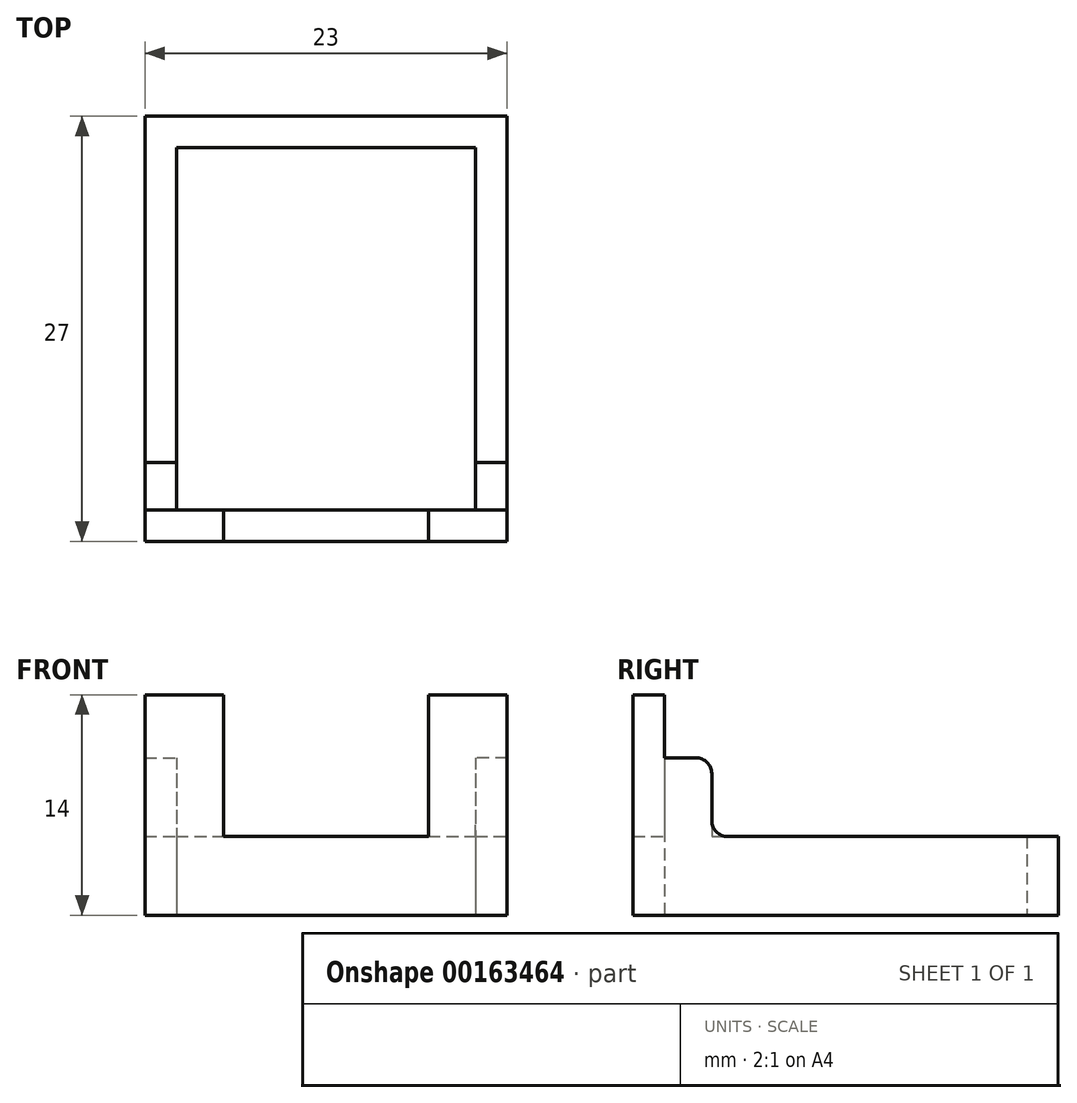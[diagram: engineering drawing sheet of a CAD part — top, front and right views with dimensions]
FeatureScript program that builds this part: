
annotation { "Feature Type Name" : "Feature", "Feature Type Description" : "" }
export const myFeature = defineFeature(function(context is Context, id is Id, definition is map)
    precondition{}
    {
        {
            var Q0;
            Q0=qCreatedBy(makeId("Top.planeOp"),FACE);
            var sketch = newSketch(context, id + "F0", { "sketchPlane" : qUnion([Q0])});
            skLineSegment(sketch, "E0", {"start": v(0, 0) * mm, "end": v(0, 23) * mm});
            skLineSegment(sketch, "E1", {"start": v(0, 0) * mm, "end": v(19, 0) * mm});
            skLineSegment(sketch, "E2", {"start": v(21, -2) * mm, "end": v(-2, -2) * mm});
            skLineSegment(sketch, "E3", {"start": v(19, 0) * mm, "end": v(19, 23) * mm});
            skLineSegment(sketch, "E4", {"start": v(0, 23) * mm, "end": v(19, 23) * mm});
            skLineSegment(sketch, "E5", {"start": v(-2, 25) * mm, "end": v(21, 25) * mm});
            skLineSegment(sketch, "E6", {"start": v(-2, -2) * mm, "end": v(-2, 25) * mm});
            skLineSegment(sketch, "E7", {"start": v(21, -2) * mm, "end": v(21, 25) * mm});
            skSolve(sketch);
        }
        {
            var Q0;
            Q0=qSketchRegion(id+"F0",true);
            extrude(context, id + "F1", {"entities" : qUnion([Q0]), "depth" : 5 * mm});
        }
        {
            var Q0;
            Q0=makeQuery(id+"F1.opExtrude","CAP_FACE",FACE,{"disambiguationData":[OSD([sQuery(id+"F0.wireOp",EDGE,"E0"),sQuery(id+"F0.wireOp",EDGE,"fMDAZUCE-WxNw-tCVg-Pr7f-gKTRDs7ux1xq"),sQuery(id+"F0.wireOp",EDGE,"E1"),sQuery(id+"F0.wireOp",EDGE,"E2"),sQuery(id+"F0.wireOp",EDGE,"em9QBzyh-X0cC-lrsQ-LOUW-UWbV2uQWN0fi"),sQuery(id+"F0.wireOp",EDGE,"E3"),sQuery(id+"F0.wireOp",EDGE,"HnKAWu8F-w6AE-VERm-Axyq-VS4Tu44atyqC"),sQuery(id+"F0.wireOp",EDGE,"QTcbnend-T0hK-HJJc-kWl9-1F0Q0khNvwRf")])],"isStart":false});
            var sketch = newSketch(context, id + "F2", { "sketchPlane" : qUnion([Q0])});
            skLineSegment(sketch, "E8", {"start": v(0, 0) * mm, "end": v(3, 0) * mm});
            skLineSegment(sketch, "E9", {"start": v(3, 0) * mm, "end": v(3, -2) * mm});
            skLineSegment(sketch, "E10", {"start": v(3, -2) * mm, "end": v(-2, -2) * mm});
            skLineSegment(sketch, "E11", {"start": v(-2, -2) * mm, "end": v(-2, 3) * mm});
            skLineSegment(sketch, "E12", {"start": v(-2, 3) * mm, "end": v(0, 3) * mm});
            skLineSegment(sketch, "E13", {"start": v(0, 3) * mm, "end": v(0, 0) * mm});
            skSolve(sketch);
        }
        {
            var Q0;
            Q0=makeQuery(id+"F2.imprint","IMPRINT",FACE,{"disambiguationData":[TD([[makeQuery(id+"F2.imprint","IMPRINT",EDGE,{"derivedFrom":sQuery(id+"F2.wireOp",EDGE,"E8")}),-1.0]])]});
            extrude(context, id + "F3", {"entities" : qUnion([Q0]), "operationType" : NewBodyOperationType.ADD, "depth" : 5 * mm});
        }
        {
            var Q0;
            {var subQ0=sQuery(id+"F0.wireOp",EDGE,"HnKAWu8F-w6AE-VERm-Axyq-VS4Tu44atyqC");var subQ1=sQuery(id+"F0.wireOp",EDGE,"E3");var subQ2=sQuery(id+"F0.wireOp",EDGE,"E2");var subQ3=sQuery(id+"F0.wireOp",EDGE,"E1");var subQ4=sQuery(id+"F0.wireOp",EDGE,"QTcbnend-T0hK-HJJc-kWl9-1F0Q0khNvwRf");Q0=makeQuery(id+"F3.boolean.opBoolean","SPLIT",FACE,{"disambiguationData":[TD([makeQuery(id+"F1.opExtrude","SWEPT_FACE",FACE,{"disambiguationData":[OSD([subQ3])]})])],"derivedFrom":makeQuery(id+"F1.opExtrude","CAP_FACE",FACE,{"disambiguationData":[OSD([sQuery(id+"F0.wireOp",EDGE,"E0"),sQuery(id+"F0.wireOp",EDGE,"fMDAZUCE-WxNw-tCVg-Pr7f-gKTRDs7ux1xq"),subQ3,subQ2,sQuery(id+"F0.wireOp",EDGE,"em9QBzyh-X0cC-lrsQ-LOUW-UWbV2uQWN0fi"),subQ1,subQ0,subQ4])],"isStart":false})});}
            var sketch = newSketch(context, id + "F4", { "sketchPlane" : qUnion([Q0])});
            skLineSegment(sketch, "E14", {"start": v(19, 0) * mm, "end": v(19, 3) * mm});
            skLineSegment(sketch, "E15", {"start": v(19, 3) * mm, "end": v(21, 3) * mm});
            skLineSegment(sketch, "E16", {"start": v(21, 3) * mm, "end": v(21, -2) * mm});
            skLineSegment(sketch, "E17", {"start": v(21, -2) * mm, "end": v(16, -2) * mm});
            skLineSegment(sketch, "E18", {"start": v(16, -2) * mm, "end": v(16, 0) * mm});
            skLineSegment(sketch, "E19", {"start": v(16, 0) * mm, "end": v(19, 0) * mm});
            skSolve(sketch);
        }
        {
            var Q0;
            Q0=makeQuery(id+"F4.imprint","IMPRINT",FACE,{"disambiguationData":[TD([[makeQuery(id+"F4.imprint","IMPRINT",EDGE,{"derivedFrom":sQuery(id+"F4.wireOp",EDGE,"E14")}),-1.0]])]});
            extrude(context, id + "F5", {"entities" : qUnion([Q0]), "operationType" : NewBodyOperationType.ADD, "depth" : 5 * mm});
        }
        {
            var Q0;
            Q0=makeQuery(id+"F3.opExtrude","CAP_FACE",FACE,{"disambiguationData":[OSD([sQuery(id+"F2.wireOp",EDGE,"E8"),sQuery(id+"F2.wireOp",EDGE,"E9"),sQuery(id+"F2.wireOp",EDGE,"E10"),sQuery(id+"F2.wireOp",EDGE,"E11"),sQuery(id+"F2.wireOp",EDGE,"E12"),sQuery(id+"F2.wireOp",EDGE,"E13")])],"isStart":false});
            var sketch = newSketch(context, id + "F6", { "sketchPlane" : qUnion([Q0])});
            skLineSegment(sketch, "E20", {"start": v(0, 0) * mm, "end": v(3, 0) * mm});
            skLineSegment(sketch, "E21", {"start": v(3, 0) * mm, "end": v(3, -2) * mm});
            skLineSegment(sketch, "E22", {"start": v(3, -2) * mm, "end": v(-2, -2) * mm});
            skLineSegment(sketch, "E23", {"start": v(-2, -2) * mm, "end": v(-2, 0) * mm});
            skLineSegment(sketch, "E24", {"start": v(-2, 0) * mm, "end": v(0, 0) * mm});
            skSolve(sketch);
        }
        {
            var Q0;
            Q0 = qSketchRegion(id + "F6", true);
            extrude(context, id + "F7", {"entities" : qUnion([Q0]), "operationType" : NewBodyOperationType.ADD, "depth" : 4 * mm});
        }
        {
            var Q0;
            Q0=makeQuery(id+"F5.opExtrude","CAP_FACE",FACE,{"disambiguationData":[OSD([sQuery(id+"F4.wireOp",EDGE,"E14"),sQuery(id+"F4.wireOp",EDGE,"E15"),sQuery(id+"F4.wireOp",EDGE,"E16"),sQuery(id+"F4.wireOp",EDGE,"E17"),sQuery(id+"F4.wireOp",EDGE,"E18"),sQuery(id+"F4.wireOp",EDGE,"E19")])],"isStart":false});
            var sketch = newSketch(context, id + "F8", { "sketchPlane" : qUnion([Q0])});
            skLineSegment(sketch, "E25", {"start": v(16, 0) * mm, "end": v(16, -2) * mm});
            skLineSegment(sketch, "E26", {"start": v(16, -2) * mm, "end": v(21, -2) * mm});
            skLineSegment(sketch, "E27", {"start": v(21, -2) * mm, "end": v(21, 0) * mm});
            skLineSegment(sketch, "E28", {"start": v(21, 0) * mm, "end": v(16, 0) * mm});
            skSolve(sketch);
        }
        {
            var Q0;
            Q0 = qSketchRegion(id + "F8", true);
            extrude(context, id + "F9", {"entities" : qUnion([Q0]), "operationType" : NewBodyOperationType.ADD, "depth" : 4 * mm});
        }
        {
            var Q0;
            Q0=makeQuery(id+"F5.opExtrude","CAP_EDGE",EDGE,{"disambiguationData":[OSD([sQuery(id+"F4.wireOp",EDGE,"E15")])],"isStart":true});
            var Q1;
            Q1=makeQuery(id+"F9.opExtrude","CAP_EDGE",EDGE,{"disambiguationData":[OSD([sQuery(id+"F8.wireOp",EDGE,"E28")])],"isStart":true});
            var Q2;
            Q2=makeQuery(id+"F5.opExtrude","CAP_EDGE",EDGE,{"disambiguationData":[OSD([sQuery(id+"F4.wireOp",EDGE,"E15")])],"isStart":false});
            var Q3;
            Q3=makeQuery(id+"F7.opExtrude","CAP_EDGE",EDGE,{"disambiguationData":[OSD([sQuery(id+"F6.wireOp",EDGE,"E20"),sQuery(id+"F6.wireOp",EDGE,"E24")])],"isStart":true});
            var Q4;
            Q4=makeQuery(id+"F3.opExtrude","CAP_EDGE",EDGE,{"disambiguationData":[OSD([sQuery(id+"F2.wireOp",EDGE,"E12")])],"isStart":false});
            var Q5;
            Q5=makeQuery(id+"F3.opExtrude","CAP_EDGE",EDGE,{"disambiguationData":[OSD([sQuery(id+"F2.wireOp",EDGE,"E12")])],"isStart":true});
            fillet(context, id + "F10", {"entities" : qUnion([Q0, Q1, Q2, Q3, Q4, Q5]), "radius" : 1 * mm, "tangentPropagation" : true, "allowEdgeOverflow" : false});
        }
    });
